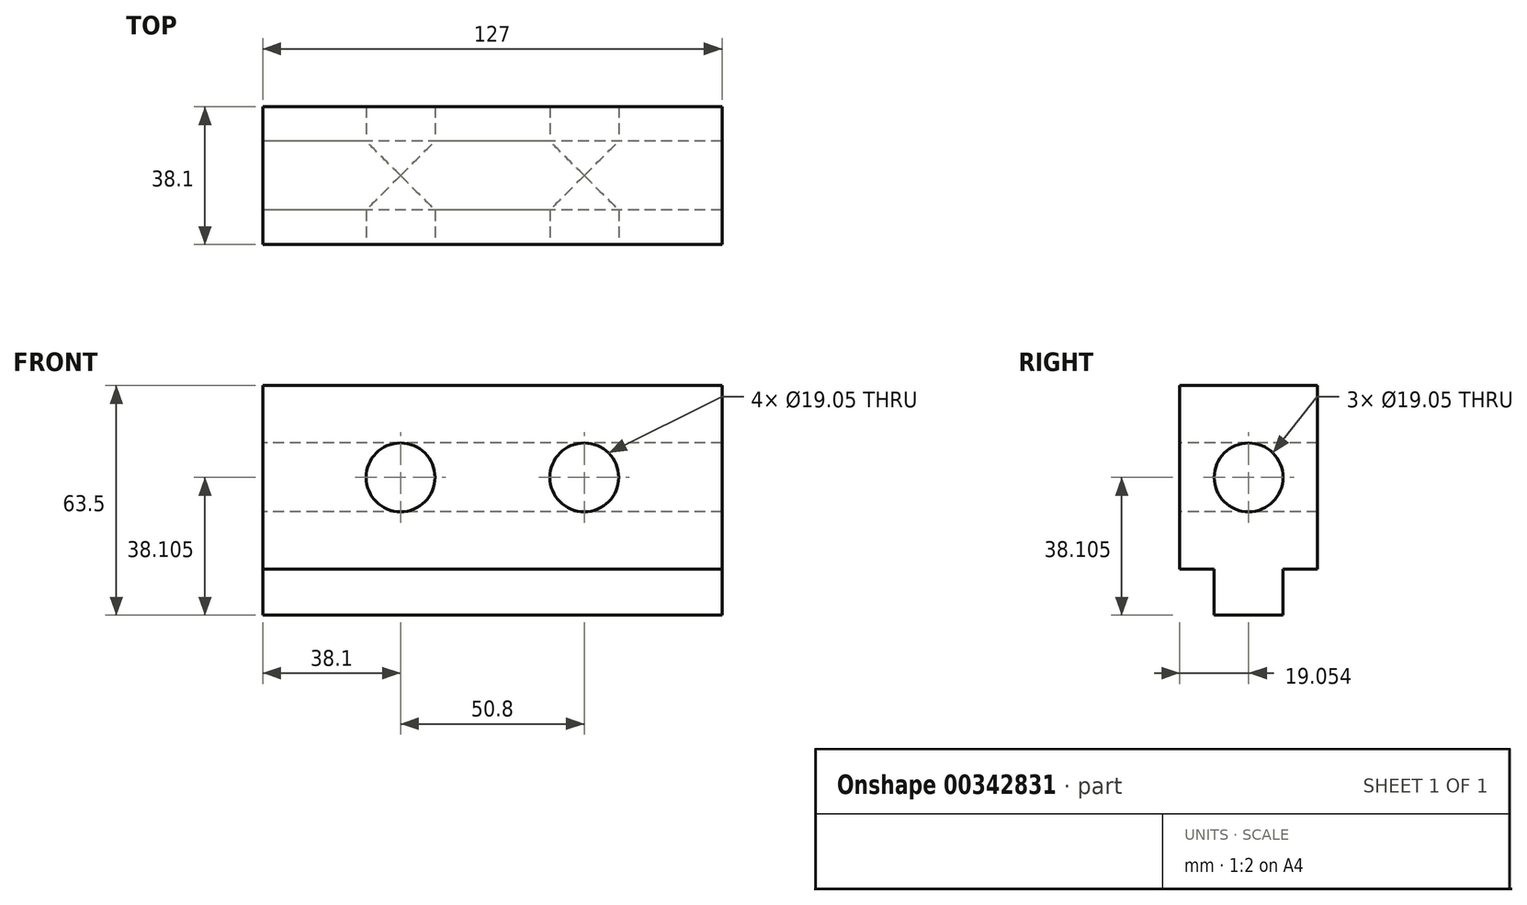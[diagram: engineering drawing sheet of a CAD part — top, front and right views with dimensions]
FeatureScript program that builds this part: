
annotation { "Feature Type Name" : "Feature", "Feature Type Description" : "" }
export const myFeature = defineFeature(function(context is Context, id is Id, definition is map)
    precondition{}
    {
        {
            var Q0;
            Q0=qCreatedBy(makeId("Right.planeOp"),FACE);
            var sketch = newSketch(context, id + "F0", { "sketchPlane" : qUnion([Q0])});
            skLineSegment(sketch, "E0", {"start": v(-18, 34.41) * mm, "end": v(20.1, 34.41) * mm});
            skLineSegment(sketch, "E1", {"start": v(20.1, 34.41) * mm, "end": v(20.1, -16.39) * mm});
            skLineSegment(sketch, "E2", {"start": v(20.1, -16.39) * mm, "end": v(10.57, -16.39) * mm});
            skLineSegment(sketch, "E3", {"start": v(10.57, -16.39) * mm, "end": v(10.57, -29.09) * mm});
            skLineSegment(sketch, "E4", {"start": v(10.57, -29.09) * mm, "end": v(-8.48, -29.09) * mm});
            skLineSegment(sketch, "E5", {"start": v(-8.48, -29.09) * mm, "end": v(-8.48, -16.39) * mm});
            skLineSegment(sketch, "E6", {"start": v(-8.48, -16.39) * mm, "end": v(-18, -16.39) * mm});
            skLineSegment(sketch, "E7", {"start": v(-18, -16.39) * mm, "end": v(-18, 34.41) * mm});
            skCircle(sketch, "E8", {"center": v(1.04, 9.01) * mm, "radius": 9.53 * mm});
            skPoint(sketch, "E8.centerSnap0", {"position": v(-18, 9.01) * mm});
            skPoint(sketch, "E8.centerSnap1", {"position": v(1.04, 34.41) * mm});
            skSolve(sketch);
        }
        {
            var Q0;
            Q0 = qSketchRegion(id + "F0", true);
            extrude(context, id + "F1", {"entities" : qUnion([Q0]), "depth" : 127 * mm});
        }
        {
            var Q0;
            Q0=makeQuery(id+"F1.opExtrude","SWEPT_FACE",FACE,{"disambiguationData":[OSD([sQuery(id+"F0.wireOp",EDGE,"E7")])]});
            var sketch = newSketch(context, id + "F2", { "sketchPlane" : qUnion([Q0])});
            skCircle(sketch, "E9", {"center": v(38.1, 9.01) * mm, "radius": 9.53 * mm});
            skCircle(sketch, "E10", {"center": v(88.9, 9.01) * mm, "radius": 9.53 * mm});
            skSolve(sketch);
        }
        {
            var Q0;
            Q0=makeQuery(id+"F2.imprint","IMPRINT",FACE,{"disambiguationData":[TD([[makeQuery(id+"F2.imprint","IMPRINT",EDGE,{"derivedFrom":sQuery(id+"F2.wireOp",EDGE,"E9")}),1.0]])]});
            var Q1;
            Q1=makeQuery(id+"F2.imprint","IMPRINT",FACE,{"disambiguationData":[TD([[makeQuery(id+"F2.imprint","IMPRINT",EDGE,{"derivedFrom":sQuery(id+"F2.wireOp",EDGE,"E10")}),1.0]])]});
            extrude(context, id + "F3", {"entities" : qUnion([Q0, Q1]), "operationType" : NewBodyOperationType.REMOVE, "oppositeDirection" : true, "depth" : 38.35 * mm});
        }
    });
